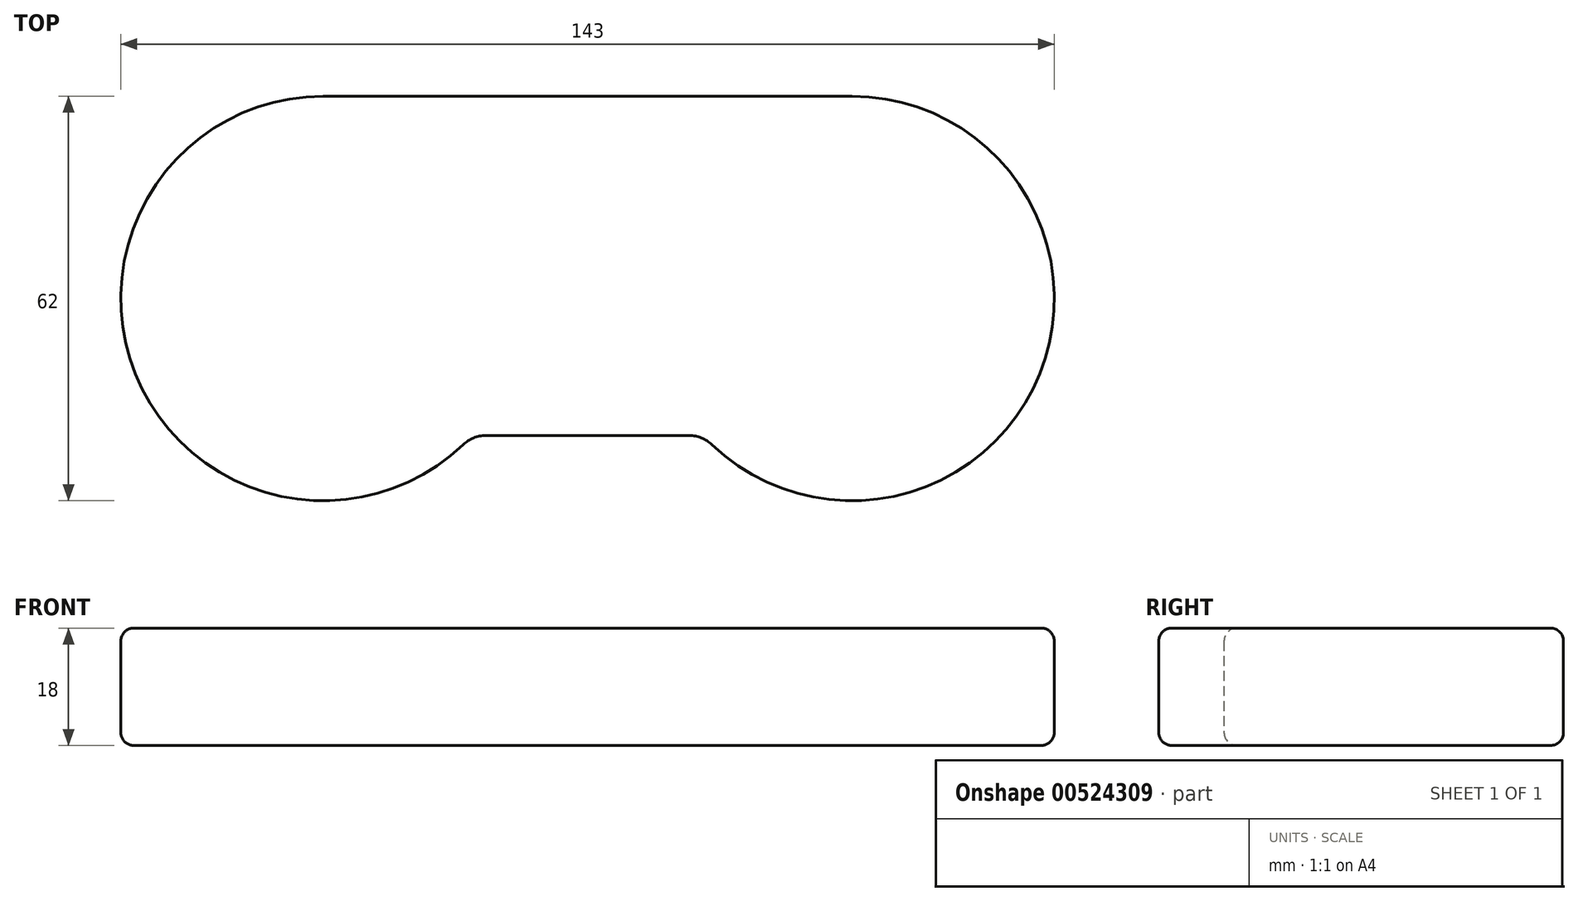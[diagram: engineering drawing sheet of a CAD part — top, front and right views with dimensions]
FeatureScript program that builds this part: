
annotation { "Feature Type Name" : "Feature", "Feature Type Description" : "" }
export const myFeature = defineFeature(function(context is Context, id is Id, definition is map)
    precondition{}
    {
        {
            var Q0;
            Q0=qCreatedBy(makeId("Top.planeOp"),FACE);
            var sketch = newSketch(context, id + "F0", { "sketchPlane" : qUnion([Q0])});
            skLineSegment(sketch, "E0", {"start": v(-38.66, 55.66) * mm, "end": v(42.34, 55.66) * mm});
            skLineSegment(sketch, "E1", {"start": v(-69.66, 24.66) * mm, "end": v(-38.66, 24.66) * mm});
            skLineSegment(sketch, "E2", {"start": v(73.34, 24.66) * mm, "end": v(42.34, 24.66) * mm});
            skArc(sketch, "E3", {"start": v(-38.66, 55.66) * mm, "mid": v(-67.05, 12.21) * mm, "end": v(-15.86, 3.66) * mm});
            skArc(sketch, "E4", {"start": v(19.54, 3.66) * mm, "mid": v(70.73, 12.21) * mm, "end": v(42.34, 55.66) * mm});
            skPoint(sketch, "E5.orphan", {"position": v(-69.66, 55.66) * mm});
            skPoint(sketch, "E6.orphan", {"position": v(-69.66, -6.34) * mm});
            skPoint(sketch, "E7.orphan", {"position": v(73.34, -6.34) * mm});
            skPoint(sketch, "E8.orphan", {"position": v(73.34, 55.66) * mm});
            skLineSegment(sketch, "E9", {"start": v(1.84, 3.66) * mm, "end": v(-15.86, 3.66) * mm});
            skLineSegment(sketch, "E10", {"start": v(1.84, 3.66) * mm, "end": v(19.54, 3.66) * mm});
            skPoint(sketch, "E11.orphan", {"position": v(-38.66, -6.34) * mm});
            skPoint(sketch, "E12.end.orphan", {"position": v(42.34, -6.34) * mm});
            skPoint(sketch, "E13.start.orphan", {"position": v(1.84, -6.34) * mm});
            skSolve(sketch);
        }
        {
            var Q0;
            {var subQ6=sQuery(id+"F0.wireOp",EDGE,"E0");Q0=makeQuery(id+"F0.imprint","IMPRINT",FACE,{"disambiguationData":[TD([[makeQuery(id+"F0.imprint","IMPRINT",EDGE,{"derivedFrom":subQ6}),-1.0]])]});}
            extrude(context, id + "F1", {"entities" : qUnion([Q0]), "depth" : 18 * mm, "offsetDistance" : 25 * mm});
        }
        {
            var Q0;
            Q0=makeQuery(id+"F1.opExtrude","SWEPT_EDGE",EDGE,{"disambiguationData":[OSD([sQuery(id+"F0.wireOp",EDGE,"E4"),sQuery(id+"F0.wireOp",EDGE,"E10")])]});
            var Q1;
            Q1=makeQuery(id+"F1.opExtrude","SWEPT_EDGE",EDGE,{"disambiguationData":[OSD([sQuery(id+"F0.wireOp",EDGE,"E3"),sQuery(id+"F0.wireOp",EDGE,"E9")])]});
            fillet(context, id + "F2", {"entities" : qUnion([Q0, Q1]), "radius" : 5 * mm, "tangentPropagation" : true, "allowEdgeOverflow" : false});
        }
        {
            var Q0;
            Q0=makeQuery(id+"F1.opExtrude","CAP_FACE",FACE,{"disambiguationData":[OSD([sQuery(id+"F0.wireOp",EDGE,"E0"),sQuery(id+"F0.wireOp",EDGE,"E3"),sQuery(id+"F0.wireOp",EDGE,"E4"),sQuery(id+"F0.wireOp",EDGE,"E9"),sQuery(id+"F0.wireOp",EDGE,"E10")])],"isStart":false});
            fillet(context, id + "F3", {"entities" : qUnion([Q0]), "radius" : 2 * mm, "tangentPropagation" : true, "allowEdgeOverflow" : false});
        }
        {
            var Q0;
            Q0=makeQuery(id+"F1.opExtrude","CAP_FACE",FACE,{"disambiguationData":[OSD([sQuery(id+"F0.wireOp",EDGE,"E0"),sQuery(id+"F0.wireOp",EDGE,"E3"),sQuery(id+"F0.wireOp",EDGE,"E4"),sQuery(id+"F0.wireOp",EDGE,"E9"),sQuery(id+"F0.wireOp",EDGE,"E10")])],"isStart":true});
            fillet(context, id + "F4", {"entities" : qUnion([Q0]), "radius" : 2 * mm, "tangentPropagation" : true, "allowEdgeOverflow" : false});
        }
    });
